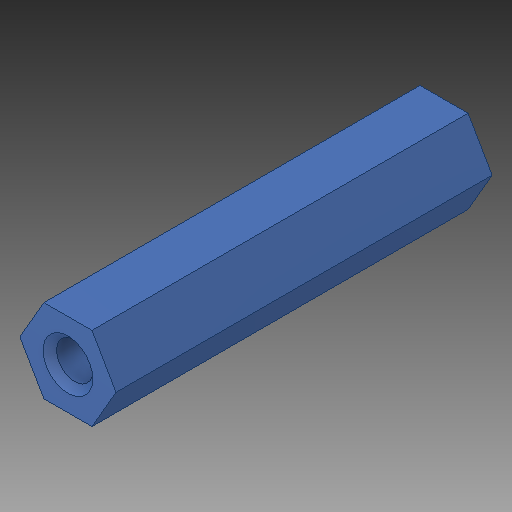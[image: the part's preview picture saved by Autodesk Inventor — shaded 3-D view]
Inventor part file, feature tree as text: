
AUTODESK INVENTOR PART (.ipt)
format: ipt  version: 2018 (Build 220112000, 112)  size: 115,712 bytes
history: native  units: in
note: dims shown in document units (in); Inventor stores cm internally (conversion verified against a paired STEP export)
features: chamfer x1
ambient origin geometry x8: Origin, YZ Plane, XZ Plane, XY Plane, X Axis, Y Axis, Z Axis, Center Point
bodies: Solid1 (feature_tree)
feature tree (1):
  chamfer  "Chamfer1"  [1 undecoded]
note: 1 required parameter value undecoded (feature->parameter linkage not recoverable at this tier; creation-order binding heuristic only, values carry confidence <= 0.55)
